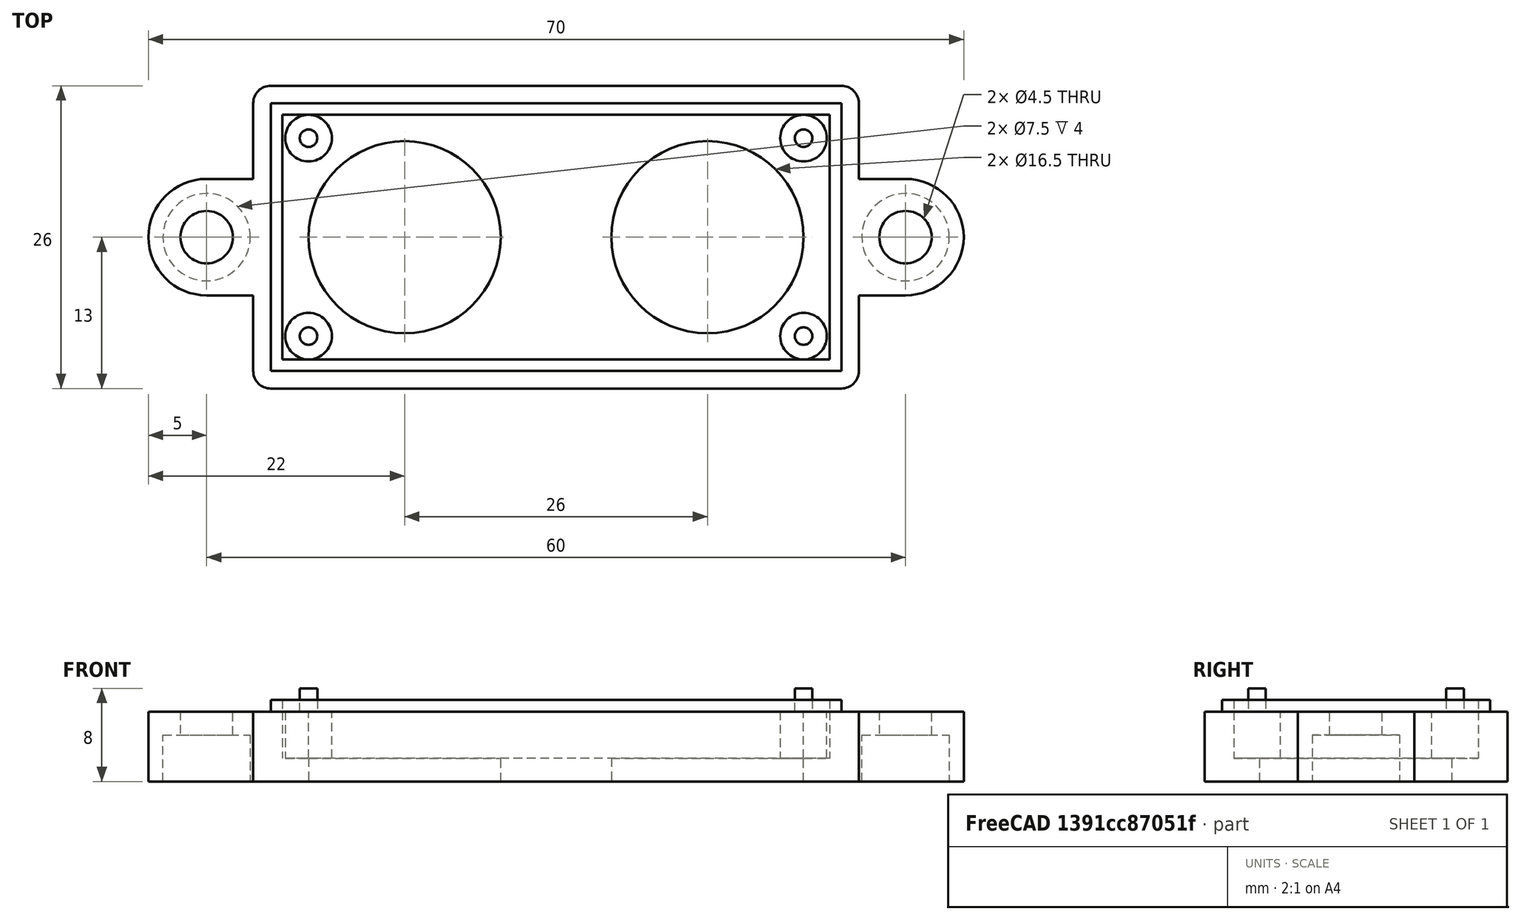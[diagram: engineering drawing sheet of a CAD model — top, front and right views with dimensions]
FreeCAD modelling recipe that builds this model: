
FCSTD DOCUMENT  (FreeCAD 1.1R44227 +322 (Git))
Label: cover
License: All rights reserved
LicenseURL: https://en.wikipedia.org/wiki/All_rights_reserved
objects: Sketcher::SketchObject×9, PartDesign::Pad×4, PartDesign::Pocket×3, PartDesign::Fillet×1, PartDesign::Body×1, App::Point×1
note: 43 computed .brp shape members not serialized (recipe doc carries the construction recipe); baked Part::Feature solids carry a one-line shape summary decoded from their .brp

FEATURE [Sketcher::SketchObject] Sketch011  label="эскиз003"
  ArcFitTolerance = 0
  ExternalTypes = [0]
  FullyConstrained = true
  MakeInternals = false
  sketch-geometry (14):
    g0: LineSegment StartX=-26 StartY=13 StartZ=0 EndX=26 EndY=13 EndZ=0
    g1: LineSegment StartX=-26 StartY=-13 StartZ=0 EndX=26 EndY=-13 EndZ=0
    g2: Circle CenterX=-30 CenterY=0 CenterZ=0 NormalX=0 NormalY=0 NormalZ=1 AngleXU=0 Radius=2.25
    g3: ArcOfCircle CenterX=-30 CenterY=0 CenterZ=0 NormalX=0 NormalY=0 NormalZ=1 AngleXU=0 Radius=5 StartAngle=1.5708 EndAngle=4.71239
    g4: LineSegment StartX=-30 StartY=5 StartZ=0 EndX=-26 EndY=5 EndZ=0
    g5: LineSegment StartX=-30 StartY=-5 StartZ=0 EndX=-26 EndY=-5 EndZ=0
    g6: Circle CenterX=30 CenterY=0 CenterZ=0 NormalX=0 NormalY=0 NormalZ=1 AngleXU=0 Radius=2.25
    g7: ArcOfCircle CenterX=30 CenterY=0 CenterZ=0 NormalX=0 NormalY=0 NormalZ=1 AngleXU=0 Radius=5 StartAngle=4.71239 EndAngle=7.85398
    g8: LineSegment StartX=30 StartY=5 StartZ=0 EndX=26 EndY=5 EndZ=0
    g9: LineSegment StartX=30 StartY=-5 StartZ=0 EndX=26 EndY=-5 EndZ=0
    g10: LineSegment StartX=-26 StartY=13 StartZ=0 EndX=-26 EndY=5 EndZ=0
    g11: LineSegment StartX=-26 StartY=-5 StartZ=0 EndX=-26 EndY=-13 EndZ=0
    g12: LineSegment StartX=26 StartY=13 StartZ=0 EndX=26 EndY=5 EndZ=0
    g13: LineSegment StartX=26 StartY=-5 StartZ=0 EndX=26 EndY=-13 EndZ=0
  constraints (43):
    c: DistanceY(g1,g0) = 26
    c: Horizontal(g0)
    c: DistanceX(g0,g0) = 52
    c: Horizontal(g1)
    c: Distance(g-1,g0) = 13
    c: PointOnObject(g2,g-1)
    c: Diameter(g2) = 4.5
    c: Distance(g-1,g2) = 30
    c: Coincident(g3,g2)
    c: Radius(g3) = 5
    c: Coincident(g4,g3)
    c: Horizontal(g4)
    c: Coincident(g5,g3)
    c: Horizontal(g5)
    c: DistanceX(g4,g4) = 4
    c: DistanceX(g5,g5) = 4
    c: PointOnObject(g6,g-1)
    c: Diameter(g6) = 4.5
    c: Distance(g-1,g6) = 30
    c: PointOnObject(g7,g-1)
    c: Radius(g7) = 5
    c: Coincident(g8,g7)
    c: Horizontal(g8)
    c: Coincident(g9,g7)
    c: Horizontal(g9)
    c: DistanceX(g8,g8) = 4
    c: DistanceX(g9,g9) = 4
    c: Distance(g-1,g8) = 5
    c: Distance(g-1,g9) = 5
    c: Coincident(g10,g0)
    c: Coincident(g10,g4)
    c: Vertical(g10)
    c: Coincident(g11,g5)
    c: Coincident(g11,g1)
    c: Vertical(g11)
    c: Coincident(g12,g0)
    c: Coincident(g12,g8)
    c: Vertical(g12)
    c: Coincident(g13,g9)
    c: Coincident(g13,g1)
    c: Vertical(g13)
    c: DistanceY(g10,g10) = 8
    c: Distance(g-1,g11) = 26
FEATURE [PartDesign::Pad] Pad004
  Direction = (0,0,1)
  Length = 6
  Length2 = 10
  Profile = -> Sketch011
  ReferenceAxis = -> Sketch011 [N_Axis]
  SideType = 0
  Suppressed = false
  Type = 0
  Type2 = 0
FEATURE [Sketcher::SketchObject] Sketch012  label="sensor001"
  ArcFitTolerance = 0
  ExternalTypes = [0]
  FullyConstrained = true
  MakeInternals = false
  sketch-geometry (2):
    g0: Circle CenterX=-13 CenterY=0 CenterZ=0 NormalX=0 NormalY=0 NormalZ=1 AngleXU=0 Radius=8.25
    g1: Circle CenterX=13 CenterY=0 CenterZ=0 NormalX=0 NormalY=0 NormalZ=1 AngleXU=0 Radius=8.25
  constraints (6):
    c: Diameter(g0) = 16.5
    c: Diameter(g1) = 16.5
    c: Distance(g-1,g0) = 13
    c: Distance(g-1,g1) = 13
    c: DistanceY(g-1,g0) = 0
    c: DistanceY(g-1,g1) = 0
FEATURE [Sketcher::SketchObject] Sketch018  label="эскиз004"
  ArcFitTolerance = 0
  ExternalTypes = [0]
  FullyConstrained = true
  MakeInternals = false
  sketch-geometry (4):
    g0: LineSegment StartX=-24 StartY=11 StartZ=0 EndX=24 EndY=11 EndZ=0
    g1: LineSegment StartX=-24 StartY=11 StartZ=0 EndX=-24 EndY=-11 EndZ=0
    g2: LineSegment StartX=24 StartY=11 StartZ=0 EndX=24 EndY=-11 EndZ=0
    g3: LineSegment StartX=-24 StartY=-11 StartZ=0 EndX=24 EndY=-11 EndZ=0
  constraints (12):
    c: Horizontal(g0)
    c: DistanceX(g0,g0) = 48
    c: Coincident(g1,g0)
    c: Vertical(g1)
    c: DistanceY(g1,g1) = 22
    c: Coincident(g2,g0)
    c: Vertical(g2)
    c: Coincident(g3,g1)
    c: Coincident(g3,g2)
    c: Horizontal(g3)
    c: Distance(g-1,g0) = 11
    c: Distance(g-1,g1) = 24
FEATURE [Sketcher::SketchObject] Sketch019  label="внутренняя фаска001"
  ArcFitTolerance = 0
  ExternalTypes = [0]
  FullyConstrained = true
  MakeInternals = false
  sketch-geometry (4):
    g0: LineSegment StartX=-25 StartY=12 StartZ=0 EndX=25 EndY=12 EndZ=0
    g1: LineSegment StartX=-25 StartY=-12 StartZ=0 EndX=25 EndY=-12 EndZ=0
    g2: LineSegment StartX=-25 StartY=-12 StartZ=0 EndX=-25 EndY=12 EndZ=0
    g3: LineSegment StartX=25 StartY=-12 StartZ=0 EndX=25 EndY=12 EndZ=0
  constraints (13):
    c: Horizontal(g0)
    c: DistanceX(g0,g0) = 50
    c: Horizontal(g1)
    c: DistanceX(g1,g1) = 50
    c: Vertical(g2)
    c: Vertical(g3)
    c: DistanceY(g2,g2) = 24
    c: DistanceY(g3,g3) = 24
    c: Coincident(g2,g1)
    c: Coincident(g2,g0)
    c: Coincident(g3,g1)
    c: Distance(g-1,g2) = 25
    c: Distance(g-1,g1) = 12
FEATURE [Sketcher::SketchObject] Sketch020  label="эскиз005"
  ArcFitTolerance = 0
  ExternalTypes = [0]
  FullyConstrained = true
  MakeInternals = false
  sketch-geometry (4):
    g0: LineSegment StartX=-23.5 StartY=10.5 StartZ=0 EndX=23.5 EndY=10.5 EndZ=0
    g1: LineSegment StartX=-23.5 StartY=10.5 StartZ=0 EndX=-23.5 EndY=-10.5 EndZ=0
    g2: LineSegment StartX=23.5 StartY=10.5 StartZ=0 EndX=23.5 EndY=-10.5 EndZ=0
    g3: LineSegment StartX=-23.5 StartY=-10.5 StartZ=0 EndX=23.5 EndY=-10.5 EndZ=0
  constraints (12):
    c: Horizontal(g0)
    c: DistanceX(g0,g0) = 47
    c: Coincident(g1,g0)
    c: Vertical(g1)
    c: DistanceY(g1,g1) = 21
    c: Coincident(g2,g0)
    c: Vertical(g2)
    c: Coincident(g3,g1)
    c: Coincident(g3,g2)
    c: Horizontal(g3)
    c: Distance(g-1,g0) = 10.5
    c: Distance(g-1,g1) = 23.5
FEATURE [Sketcher::SketchObject] Sketch021
  ArcFitTolerance = 0
  ExternalTypes = [0]
  FullyConstrained = true
  MakeInternals = false
  sketch-geometry (8):
    g0: LineSegment StartX=-24.5 StartY=11.5 StartZ=0 EndX=24.5 EndY=11.5 EndZ=0
    g1: LineSegment StartX=-24.5 StartY=-11.5 StartZ=0 EndX=24.5 EndY=-11.5 EndZ=0
    g2: LineSegment StartX=-24.5 StartY=-11.5 StartZ=0 EndX=-24.5 EndY=11.5 EndZ=0
    g3: LineSegment StartX=24.5 StartY=-11.5 StartZ=0 EndX=24.5 EndY=11.5 EndZ=0
    g4: LineSegment StartX=-23.5 StartY=10.5 StartZ=0 EndX=23.5 EndY=10.5 EndZ=0
    g5: LineSegment StartX=-23.5 StartY=10.5 StartZ=0 EndX=-23.5 EndY=-10.5 EndZ=0
    g6: LineSegment StartX=23.5 StartY=10.5 StartZ=0 EndX=23.5 EndY=-10.5 EndZ=0
    g7: LineSegment StartX=-23.5 StartY=-10.5 StartZ=0 EndX=23.5 EndY=-10.5 EndZ=0
  constraints (25):
    c: Horizontal(g0)
    c: DistanceX(g0,g0) = 49
    c: Horizontal(g1)
    c: DistanceX(g1,g1) = 49
    c: Vertical(g2)
    c: Vertical(g3)
    c: DistanceY(g2,g2) = 23
    c: DistanceY(g3,g3) = 23
    c: Coincident(g2,g1)
    c: Coincident(g2,g0)
    c: Coincident(g3,g1)
    c: Distance(g-1,g2) = 24.5
    c: Distance(g-1,g1) = 11.5
    c: Horizontal(g4)
    c: DistanceX(g4,g4) = 47
    c: Coincident(g5,g4)
    c: Vertical(g5)
    c: DistanceY(g5,g5) = 21
    c: Coincident(g6,g4)
    c: Vertical(g6)
    c: Coincident(g7,g5)
    c: Coincident(g7,g6)
    c: Horizontal(g7)
    c: Distance(g-1,g4) = 10.5
    c: Distance(g-1,g5) = 23.5
FEATURE [PartDesign::Pad] Pad005
  BaseFeature = -> Pad004
  Direction = (0,0,1)
  Length = 2
  Length2 = 10
  Profile = -> Sketch021
  ReferenceAxis = -> Sketch021 [N_Axis]
  SideType = 2
  Suppressed = false
  Type = 0
  Type2 = 0
FEATURE [PartDesign::Pocket] Pocket005
  AlongSketchNormal = false
  BaseFeature = -> Pad005
  Direction = (0,0,-1)
  Length = 0
  Length2 = 4
  Profile = -> Sketch020
  ReferenceAxis = -> Sketch020 [N_Axis]
  SideType = 1
  Suppressed = false
  Type = 0
  Type2 = 0
FEATURE [PartDesign::Pocket] Pocket006
  BaseFeature = -> Pocket005
  Direction = (0,0,-1)
  Length = 8
  Length2 = 8
  Profile = -> Sketch012
  ReferenceAxis = -> Sketch012 [N_Axis]
  SideType = 1
  Suppressed = false
  Type = 0
  Type2 = 0
FEATURE [Sketcher::SketchObject] Sketch022
  ArcFitTolerance = 0
  AttachmentSupport = -> [Pocket006]
  ExternalTypes = [0]
  FullyConstrained = true
  MakeInternals = false
  MapMode = 5
  Placement = pos=(0,0,6) rot=(0,0,1;0rad)
  sketch-geometry (2):
    g0: Circle CenterX=-30 CenterY=0 CenterZ=0 NormalX=0 NormalY=0 NormalZ=1 AngleXU=0 Radius=3.75
    g1: Circle CenterX=30 CenterY=0 CenterZ=0 NormalX=0 NormalY=0 NormalZ=1 AngleXU=0 Radius=3.75
  constraints (6):
    c: PointOnObject(g0,g-1)
    c: Diameter(g0) = 7.5
    c: Distance(g-1,g0) = 30
    c: PointOnObject(g1,g-1)
    c: Diameter(g1) = 7.5
    c: Distance(g-1,g1) = 30
FEATURE [PartDesign::Pocket] Pocket007
  BaseFeature = -> Pocket006
  Direction = (0,0,-1)
  Length = 4
  Length2 = 5
  Profile = -> Sketch022
  ReferenceAxis = -> Sketch022 [N_Axis]
  SideType = 0
  Suppressed = false
  Type = 0
  Type2 = 0
FEATURE [Sketcher::SketchObject] Sketch024  label="эскиз006"
  ArcFitTolerance = 0
  ExternalTypes = [0]
  FullyConstrained = true
  MakeInternals = false
  sketch-geometry (4):
    g0: Circle CenterX=21.25 CenterY=8.5 CenterZ=0 NormalX=0 NormalY=0 NormalZ=1 AngleXU=0 Radius=2
    g1: Circle CenterX=-21.25 CenterY=8.5 CenterZ=0 NormalX=0 NormalY=0 NormalZ=1 AngleXU=0 Radius=2
    g2: Circle CenterX=-21.25 CenterY=-8.5 CenterZ=0 NormalX=0 NormalY=0 NormalZ=1 AngleXU=0 Radius=2
    g3: Circle CenterX=21.25 CenterY=-8.5 CenterZ=0 NormalX=0 NormalY=0 NormalZ=1 AngleXU=0 Radius=2
  constraints (9):
    c: Diameter(g0) = 4
    c: Diameter(g1) = 4
    c: Diameter(g2) = 4
    c: Diameter(g3) = 4
    c: DistanceX(g-2,g1) = -21.25
    c: DistanceY(g-1,g1) = 8.5
    c: Symmetric(g1,g0,g-2)
    c: Symmetric(g1,g2,g-1)
    c: Symmetric(g2,g3,g-2)
FEATURE [PartDesign::Pad] Pad006
  BaseFeature = -> Pocket007
  Direction = (0,0,1)
  Length = 6
  Length2 = 10
  Profile = -> Sketch024
  ReferenceAxis = -> Sketch024 [N_Axis]
  SideType = 0
  Suppressed = false
  Type = 0
  Type2 = 0
FEATURE [Sketcher::SketchObject] Sketch025  label="эскиз007"
  ArcFitTolerance = 0
  ExternalTypes = [0]
  FullyConstrained = true
  MakeInternals = false
  sketch-geometry (4):
    g0: Circle CenterX=-21.25 CenterY=8.5 CenterZ=0 NormalX=0 NormalY=0 NormalZ=1 AngleXU=0 Radius=0.75
    g1: Circle CenterX=-21.25 CenterY=-8.5 CenterZ=0 NormalX=0 NormalY=0 NormalZ=1 AngleXU=0 Radius=0.75
    g2: Circle CenterX=21.25 CenterY=8.5 CenterZ=0 NormalX=0 NormalY=0 NormalZ=1 AngleXU=0 Radius=0.75
    g3: Circle CenterX=21.25 CenterY=-8.5 CenterZ=0 NormalX=0 NormalY=0 NormalZ=1 AngleXU=0 Radius=0.75
  constraints (9):
    c: Diameter(g0) = 1.5
    c: Diameter(g1) = 1.5
    c: Diameter(g2) = 1.5
    c: Diameter(g3) = 1.5
    c: DistanceX(g-2,g0) = -21.25
    c: Distance(g0,g-1) = 8.5
    c: Symmetric(g0,g2,g-2)
    c: Symmetric(g0,g1,g-1)
    c: Symmetric(g1,g3,g-2)
FEATURE [PartDesign::Pad] Pad007
  BaseFeature = -> Pad006
  Direction = (0,0,1)
  Length = 0
  Length2 = 2
  Profile = -> Sketch025
  ReferenceAxis = -> Sketch025 [N_Axis]
  SideType = 1
  Suppressed = false
  Type = 0
  Type2 = 0
FEATURE [PartDesign::Fillet] Fillet001
  Base = -> Pad007 [Edge44,Edge47,Edge8,Edge45]
  BaseFeature = -> Pad007
  Radius = 1.5
  SupportTransform = false
  Suppressed = false
  UseAllEdges = false
FEATURE [PartDesign::Body] Body001  label="hc-sr04-cover"
  AllowCompound = false
  Group = -> [Sketch011,Sketch012,Sketch018,Sketch019,Pad004,Sketch020,Sketch021,Pad005,Pocket005,Pocket006,Sketch022,Pocket007,Sketch024,Sketch025,Pad006,Pad007,Fillet001]
  Origin = -> Origin001
  Placement = pos=(0,0,-18) rot=(0,1,0;3.14159rad)
  Tip = -> Fillet001
FEATURE [App::Point] Origin
  Role = Origin
